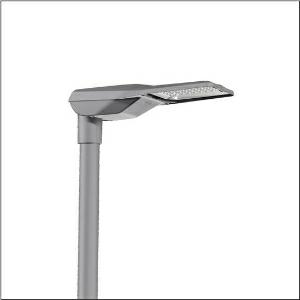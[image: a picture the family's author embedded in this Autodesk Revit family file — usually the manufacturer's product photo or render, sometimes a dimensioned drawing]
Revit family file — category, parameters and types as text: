
# Revit family: streetlight_sl_21_iq_mini___stw1_0a_5xe2e41g08gb_cbe1
name_source: partatom
category: Lighting Fixtures
units: mm (PartAtom-declared; Revit-internal decimal feet)

## family parameters
Cut with Voids When Loaded = No
Host = Face
Light Source = No
Part Type = Normal
Room Calculation Point = No
Round Connector Dimension = Use Diameter
Shared = No

## types (1)
- --- (1 x LED, 5920 lm, 37.1 W, 4000K)
    Apparent Load = 37 VA
    CIE Flux Codes = 38 75 98 100 100
    Color Rendering = 70
    Color Temperature = 4000K
    Default Elevation = 1800 mm
    Description = Streetlight SL 21 mini, mast luminaire, primary light control with lens, of PMMA, primary optical cover: cover, of toughened safety glass, transparent, light distribution: STW1.0a, light emission: direct distribution, primary light characteristic: asymmetric, installation type: post-top, side-entry, LED, High Power LED, rated luminous flux: 5.920lm, luminous efficacy: 160lm/W, light colour: 740, colour temperature: 4000K, control gear: ECG iQ, control: Street-Remote, Auto-Match, Temp-Guard, Lumen-Switch, Night-Set, Smart-Wire, Light-Fading, Desk-Remote (wireless, voltage-free reading and setting of iQ features in the workshop via application-optimized NFC function/RFID function), optimised constant luminous flux control (CLO 2.0), mains connection: 220..240V, AC, 50/60Hz, start of lifetime: 37W, end of lifetime: 39W, reduction: 18W, luminaire housing, of diecast aluminium, powder-coated, Siteco® metallic grey (DB 702S), corrosivity category C5 according to DIN EN ISO 12944, length: 628mm, width: 235mm, height: 110mm, spigot size: 60/76mm (post-top) and 42/60/76mm (side-entry), mast flange for spigot size: 42mm: 5XC10008XM4, 60mm: 5XC10008XM2, 76/60mm: 5XC10108XM1, protection rating (complete): IP66, insulation class (complete): insulation class II (safety insulation), certification: CE, ENEC, VDE, impact resistance: IK09, permissible operating ambient temperature for outdoor applications: -40..+50°C, standard-compliant lighting for roads and squares, packaging unit: 1 piece

Light Distribution: STW1.0a
    Height = 110 mm
    Lamp = 1 x LED
    Lamp Light Flux = 5920 lm
    Lamp Power = 37.1 W
    Lamp count = 1
    Length = 625 mm
    Luminous efficacy = 160 lm/W
    Manufacturer = Siteco
    ModVariant = No
    Model = 5XE2E41G08GB
    Number of Poles = 1
    OnlyDefault = Yes
    Power Factor = 1
    Product Name = Streetlight SL 21 iQ mini | STW1.0a
    Product group = mast luminaire | pylon top
    ProductGroupID = 6100
    Protection Class = Protection class II
    Protection Degree = IP 66
    RLX_Detail_Level = 1
    RlxData = <blob elided: 92025 chars, md5=c57676b2>
    Socket = socket
    Standby Power = 0 W
    System Light Flux = 5920 lm
    System Power = 37 W
    Type Comments = factory setting: luminous flux: 100 % | dim-lin: 254 | 385 mA
    Type Image = l_1003519.jpg
    URL = http://relux.com
    VarID = @adj_104851
    Voltage = 0 V
    Weight = 0.00 kg
    Width = 234 mm

## geometry (parser evidence)
native form markers: Blend x4, Sweep x10
no freeform markers — native parametric forms only
